# Revit family: ЭВАН ЭПО 2,5-30 кВт
name_source: partatom
category: Оборудование
units: mm (PartAtom-declared; Revit-internal decimal feet)

## family parameters
Всегда вертикально = Да
Классификация = Нет
На основе рабочей плоскости = Да
Общий = Нет
При загрузке вырезать с полостями = Нет
Размер круглого соединителя = Использовать диаметр
Тип детали = Нормальный
Точка расчета площади = Нет

## types (11) — shared parameters
ADSK_Классификация нагрузок = Прочее
ADSK_Материал = Сталь
ADSK_Номинальная мощность = 0 Вт
ADSK_Расход теплоносителя = 0.0 м³/ч
Dn = 32 мм
База = ЭЛЕКТРИЧЕСКИЙ ТЕПЛОГЕНЕРАТОР (КОТЕЛ)
Диапазон регулируемых температур теплоносителя, оС = От +30 до +85
Крышка_Видимость = Да
Максимальная температура теплоносителя, оС = +85
Материал корпуса = Сталь
Минимальная температура теплоносителя, оС = +30
Мощность 1-й ступени (по умолчанию) = 0 Вт
Рабоча зона_Видимость = Да
Рабочее давление, МПа = 0.1-0.3
Резьба патрубков для подключения трубопроводов теплоносителя = G1 1/4
zero-valued in all types: Отметка по умолчанию

## per-type parameters (varying)
| type | ADSK_Количество фаз | ADSK_Размер_Высота | ADSK_Размер_Длина | ADSK_Размер_Ширина | Объем колбы котла, л | Потребляемая электрическая мощность при максимальной тепловой мощность  в час, кВт/ч |
| ЭВАН ЭПО - 2,5 кВт | 1 | 229 мм | 557 мм | 220 мм | 42 | 2.63 |
| ЭВАН ЭПО - 4 кВт | 1 | 331 мм | 220 мм | 390 мм | 7.5 | 4.2 |
| ЭВАН ЭПО - 6 кВт | 1 | 331 мм | 220 мм | 390 мм | 7.5 | 6.3 |
| ЭВАН ЭПО - 7.5 кВт | 1 | 331 мм | 220 мм | 390 мм | 7.5 | 7.9 |
| ЭВАН ЭПО - 9.45 кВт 220 В | 1 | 331 мм | 220 мм | 390 мм | 7.5 | 9.9 |
| ЭВАН ЭПО - 9,45 кВт 380 В | 3 | 331 мм | 220 мм | 390 мм | 7.5 | 9.9 |
| ЭВАН ЭПО - 12 кВт | 3 | 331 мм | 220 мм | 390 мм | 7.5 | 12.6 |
| ЭВАН ЭПО - 15 кВт | 3 | 331 мм | 220 мм | 390 мм | 7.5 | 22.02 |
| ЭВАН ЭПО - 18 кВт | 3 | 331 мм | 220 мм | 390 мм | 7.5 | 19.8 |
| ЭВАН ЭПО - 24 кВт | 3 | 331 мм | 220 мм | 390 мм | 7.5 | 25.2 |
| ЭВАН ЭПО - 30 кВт | 3 | 331 мм | 220 мм | 390 мм | 7.5 | 31.5 |
